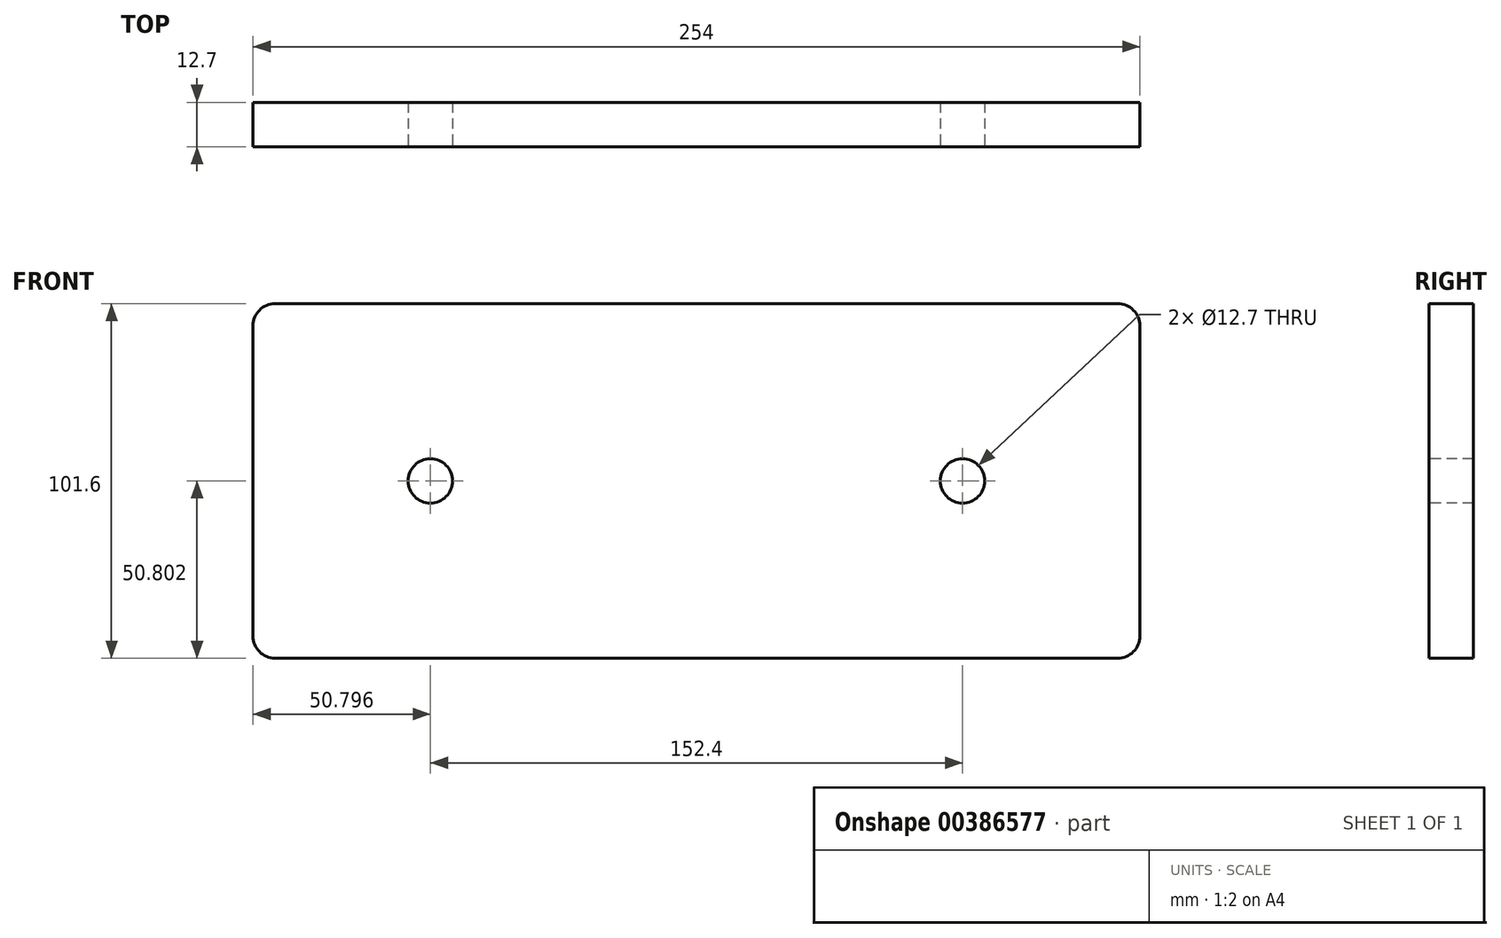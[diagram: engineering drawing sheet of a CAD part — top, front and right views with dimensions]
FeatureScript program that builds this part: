
annotation { "Feature Type Name" : "Feature", "Feature Type Description" : "" }
export const myFeature = defineFeature(function(context is Context, id is Id, definition is map)
    precondition{}
    {
        {
            var Q0;
            Q0=qCreatedBy(makeId("Front.planeOp"),FACE);
            var sketch = newSketch(context, id + "F0", { "sketchPlane" : qUnion([Q0])});
            skLineSegment(sketch, "E0", {"start": v(-85.01, 51.56) * mm, "end": v(-85.01, -50.04) * mm});
            skLineSegment(sketch, "E1", {"start": v(-85.01, -50.04) * mm, "end": v(168.99, -50.04) * mm});
            skLineSegment(sketch, "E2", {"start": v(168.99, -50.04) * mm, "end": v(168.99, 51.56) * mm});
            skLineSegment(sketch, "E3", {"start": v(168.99, 51.56) * mm, "end": v(-85.01, 51.56) * mm});
            skSolve(sketch);
        }
        {
            var Q0;
            Q0 = qSketchRegion(id + "F0", true);
            extrude(context, id + "F1", {"entities" : qUnion([Q0]), "depth" : 12.7 * mm});
        }
        {
            var Q0;
            Q0=makeQuery(id+"F1.opExtrude","SWEPT_EDGE",EDGE,{"disambiguationData":[OSD([sQuery(id+"F0.wireOp",EDGE,"E0"),sQuery(id+"F0.wireOp",EDGE,"E3")])]});
            var Q1;
            Q1=makeQuery(id+"F1.opExtrude","SWEPT_EDGE",EDGE,{"disambiguationData":[OSD([sQuery(id+"F0.wireOp",EDGE,"E2"),sQuery(id+"F0.wireOp",EDGE,"E3")])]});
            var Q2;
            Q2=makeQuery(id+"F1.opExtrude","SWEPT_EDGE",EDGE,{"disambiguationData":[OSD([sQuery(id+"F0.wireOp",EDGE,"E1"),sQuery(id+"F0.wireOp",EDGE,"E2")])]});
            var Q3;
            Q3=makeQuery(id+"F1.opExtrude","SWEPT_EDGE",EDGE,{"disambiguationData":[OSD([sQuery(id+"F0.wireOp",EDGE,"E0"),sQuery(id+"F0.wireOp",EDGE,"E1")])]});
            fillet(context, id + "F2", {"entities" : qUnion([Q0, Q1, Q2, Q3]), "radius" : 6.35 * mm, "tangentPropagation" : true, "allowEdgeOverflow" : false});
        }
        {
            var Q0;
            Q0=makeQuery(id+"F1.opExtrude","CAP_FACE",FACE,{"disambiguationData":[OSD([sQuery(id+"F0.wireOp",EDGE,"E0"),sQuery(id+"F0.wireOp",EDGE,"E1"),sQuery(id+"F0.wireOp",EDGE,"E2"),sQuery(id+"F0.wireOp",EDGE,"E3")])],"isStart":false});
            var sketch = newSketch(context, id + "F3", { "sketchPlane" : qUnion([Q0])});
            skPoint(sketch, "E4", {"position": v(-34.21, 0.76) * mm});
            skPoint(sketch, "E5.MirrorP", {"position": v(118.19, 0.76) * mm});
            skSolve(sketch);
        }
        {
            var Q0;
            Q0=sQuery(id+"F3.wireOp",VERTEX,"E4");
            var Q1;
            Q1=sQuery(id+"F3.wireOp",VERTEX,"E5.MirrorP");
            var Q2;
            Q2=makeQuery(id+"F1.opExtrude","SWEPT_BODY",BODY,{"disambiguationData":[OSD([sQuery(id+"F0.wireOp",EDGE,"E0"),sQuery(id+"F0.wireOp",EDGE,"E1"),sQuery(id+"F0.wireOp",EDGE,"E2"),sQuery(id+"F0.wireOp",EDGE,"E3")])]});
            hole(context, id + "F4", {"style" : HoleStyle.SIMPLE, "endStyle" : HoleEndStyle.THROUGH, "holeDiameter" : 12.7 * mm, "isTappedThrough" : true, "tappedDepth" : 12.7 * mm, "tapClearance" : 3, "locations" : qUnion([Q0, Q1]), "scope" : qUnion([Q2])});
        }
    });
